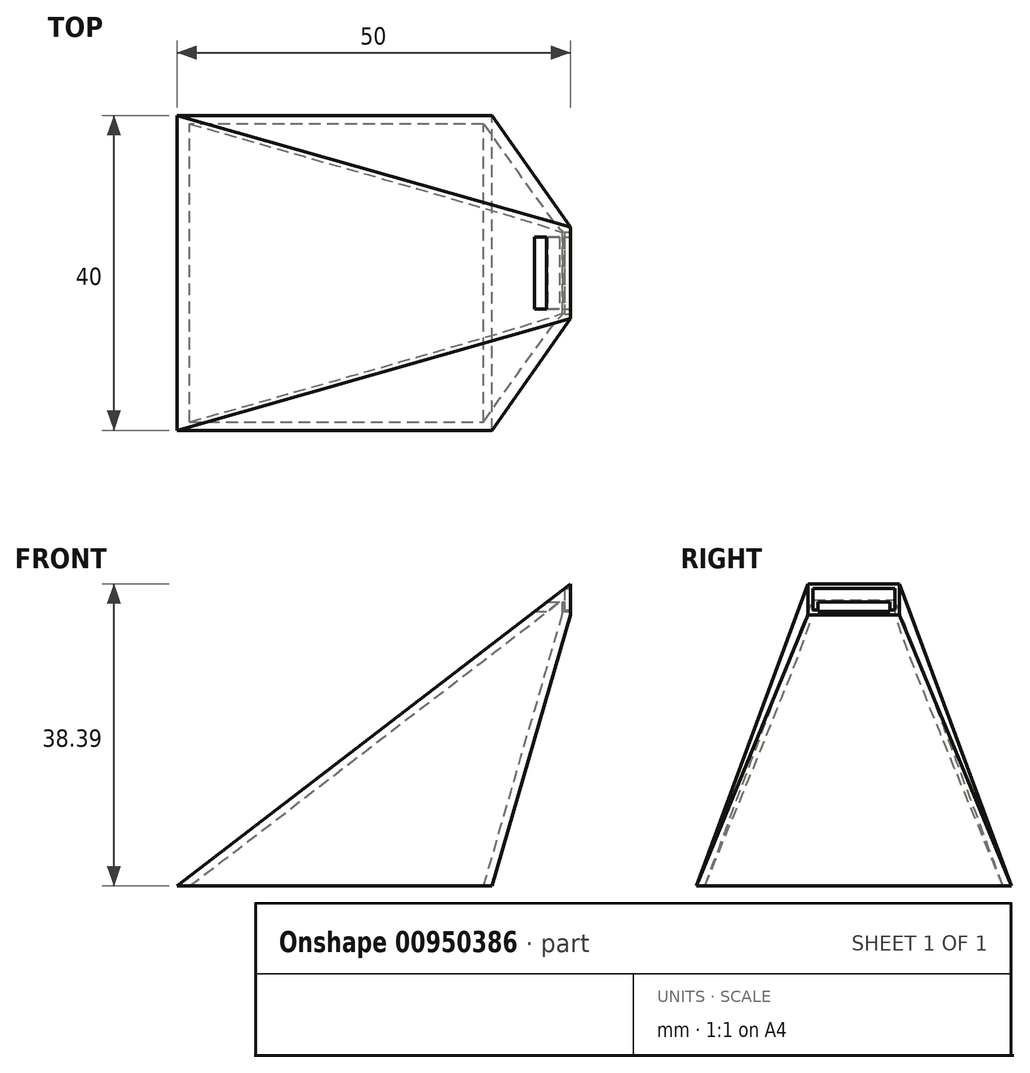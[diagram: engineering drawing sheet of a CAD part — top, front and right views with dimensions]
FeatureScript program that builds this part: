
annotation { "Feature Type Name" : "Feature", "Feature Type Description" : "" }
export const myFeature = defineFeature(function(context is Context, id is Id, definition is map)
    precondition{}
    {
        {
            var Q0;
            Q0=qCreatedBy(makeId("Right.planeOp"),FACE);
            cPlane(context, id + "F0", {"entities" : qUnion([Q0]), "cplaneType" : CPlaneType.OFFSET, "offset" : 30 * mm, "width" : 150 * mm, "height" : 150 * mm});
        }
        {
            var Q0;
            Q0=qCreatedBy(id+"F0.planeOp",FACE);
            var sketch = newSketch(context, id + "F1", { "sketchPlane" : qUnion([Q0])});
            skLineSegment(sketch, "E0.bottom", {"start": v(5.81, 34.45) * mm, "end": v(-5.81, 34.45) * mm});
            skLineSegment(sketch, "E0.top", {"start": v(5.81, 38.4) * mm, "end": v(-5.81, 38.4) * mm});
            skLineSegment(sketch, "E0.left", {"start": v(5.81, 34.45) * mm, "end": v(5.81, 38.4) * mm});
            skLineSegment(sketch, "E0.right", {"start": v(-5.81, 34.45) * mm, "end": v(-5.81, 38.4) * mm});
            skPoint(sketch, "E0.middle", {"position": v(0, 36.42) * mm});
            skSolve(sketch);
        }
        {
            var Q0;
            Q0=qCreatedBy(makeId("Top.planeOp"),FACE);
            var sketch = newSketch(context, id + "F2", { "sketchPlane" : qUnion([Q0])});
            skLineSegment(sketch, "E1.bottom", {"start": v(-20, -20) * mm, "end": v(20, -20) * mm});
            skLineSegment(sketch, "E1.top", {"start": v(-20, 20) * mm, "end": v(20, 20) * mm});
            skLineSegment(sketch, "E1.left", {"start": v(-20, -20) * mm, "end": v(-20, 20) * mm});
            skLineSegment(sketch, "E1.right", {"start": v(20, -20) * mm, "end": v(20, 20) * mm});
            skPoint(sketch, "E1.middle", {"position": v(0, 0) * mm});
            skSolve(sketch);
        }
        {
            var Q0;
            Q0=makeQuery(id+"F2.imprint","IMPRINT",FACE,{"disambiguationData":[TD([[makeQuery(id+"F2.imprint","IMPRINT",EDGE,{"derivedFrom":sQuery(id+"F2.wireOp",EDGE,"E1.bottom")}),1.0]])]});
            var Q1;
            Q1=makeQuery(id+"F1.imprint","IMPRINT",FACE,{"disambiguationData":[TD([[makeQuery(id+"F1.imprint","IMPRINT",EDGE,{"derivedFrom":sQuery(id+"F1.wireOp",EDGE,"E0.bottom")}),-1.0]])]});
            loft(context, id + "F3", {"sheetProfilesArray" : [{ "sheetProfileEntities" : qUnion([Q0]) }, { "sheetProfileEntities" : qUnion([Q1]) }]});
        }
        {
            var Q0;
            Q0=makeQuery(id+"F3.opLoft","CAP_FACE",FACE,{"disambiguationData":[OSD([makeQuery(id+"F2.imprint","IMPRINT",FACE,{"disambiguationData":[TD([[makeQuery(id+"F2.imprint","IMPRINT",EDGE,{"derivedFrom":sQuery(id+"F2.wireOp",EDGE,"E1.bottom")}),1.0]])]})])],"isStart":true});
            shell(context, id + "F4", {"entities" : qUnion([Q0]), "thickness" : 1 * mm});
        }
        {
            var Q0;
            Q0=makeQuery(id+"F1.imprint","IMPRINT",FACE,{"disambiguationData":[TD([[makeQuery(id+"F1.imprint","IMPRINT",EDGE,{"derivedFrom":sQuery(id+"F1.wireOp",EDGE,"E0.bottom")}),-1.0]])]});
            var sketch = newSketch(context, id + "F5", { "sketchPlane" : qUnion([Q0])});
            skLineSegment(sketch, "E2.bottom", {"start": v(5.2, 37.78) * mm, "end": v(-5.2, 37.78) * mm});
            skLineSegment(sketch, "E2.top", {"start": v(5.2, 35.07) * mm, "end": v(-5.2, 35.07) * mm});
            skLineSegment(sketch, "E2.left", {"start": v(5.2, 37.78) * mm, "end": v(5.2, 35.07) * mm});
            skLineSegment(sketch, "E2.right", {"start": v(-5.2, 37.78) * mm, "end": v(-5.2, 35.07) * mm});
            skPoint(sketch, "E2.middle", {"position": v(0, 36.43) * mm});
            skSolve(sketch);
        }
        {
            var Q0;
            Q0=makeQuery(id+"F5.imprint","IMPRINT",FACE,{"disambiguationData":[TD([[makeQuery(id+"F5.imprint","IMPRINT",EDGE,{"derivedFrom":sQuery(id+"F5.wireOp",EDGE,"E2.bottom")}),1.0]])]});
            extrude(context, id + "F6", {"entities" : qUnion([Q0]), "operationType" : NewBodyOperationType.REMOVE, "endBound" : BoundingType.SYMMETRIC, "oppositeDirection" : true, "depth" : 1.5 * mm, "offsetDistance" : 25 * mm});
        }
        {
            var Q0;
            Q0=makeQuery(id+"F4.opShell","OFFSET_FACE",FACE,{"disambiguationData":[OSD([makeQuery(id+"F1.imprint","IMPRINT",FACE,{"disambiguationData":[TD([[makeQuery(id+"F1.imprint","IMPRINT",EDGE,{"derivedFrom":sQuery(id+"F1.wireOp",EDGE,"E0.bottom")}),-1.0]])]})])]});
            var sketch = newSketch(context, id + "F7", { "sketchPlane" : qUnion([Q0])});
            skLineSegment(sketch, "E3.bottom", {"start": v(-4.56, 36.06) * mm, "end": v(4.56, 36.06) * mm});
            skLineSegment(sketch, "E3.top", {"start": v(-4.56, 34.9) * mm, "end": v(4.56, 34.9) * mm});
            skLineSegment(sketch, "E3.left", {"start": v(-4.56, 36.06) * mm, "end": v(-4.56, 34.9) * mm});
            skLineSegment(sketch, "E3.right", {"start": v(4.56, 36.06) * mm, "end": v(4.56, 34.9) * mm});
            skPoint(sketch, "E3.middle", {"position": v(0, 35.48) * mm});
            skPoint(sketch, "E3.middle.positionSnap0", {"position": v(0, 34.59) * mm});
            skPoint(sketch, "E3.centerSnap0", {"position": v(0, 34.59) * mm});
            skSolve(sketch);
        }
        {
            var Q0;
            Q0=makeQuery(id+"F7.imprint","IMPRINT",FACE,{"disambiguationData":[TD([[makeQuery(id+"F7.imprint","IMPRINT",EDGE,{"derivedFrom":sQuery(id+"F7.wireOp",EDGE,"E3.bottom")}),-1.0]])]});
            extrude(context, id + "F8", {"entities" : qUnion([Q0]), "operationType" : NewBodyOperationType.REMOVE, "endBound" : BoundingType.SYMMETRIC, "depth" : 25 * mm, "offsetDistance" : 25 * mm});
        }
    });
